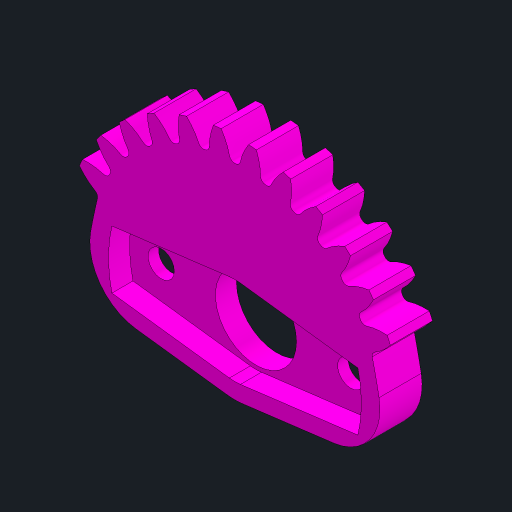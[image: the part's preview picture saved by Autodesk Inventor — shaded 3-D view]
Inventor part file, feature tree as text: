
AUTODESK INVENTOR PART (.ipt)
format: ipt  version: 2023.2 (Build 272271030, 271C)  size: 692,736 bytes
history: native  units: mm
features: extrude x5, sketch x4, pattern_circular x1, hole x1, projected_geometry x1
ambient origin geometry x8: Origin, YZ Plane, XZ Plane, XY Plane, X Axis, Y Axis, Z Axis, Center Point
bodies: Solid1 (feature_tree)
feature tree (12):
  sketch  "Sketch1"  dims[d0=4.0mm d1=0.0mm d2=0.0mm d3=0.0mm]
  extrude  "Extrusion1"  TaperAngle=0.0deg  [1 undecoded]
  extrude  "Extrusion2"  Depth=8.0mm
  pattern_circular  "Circular Pattern1"  [2 undecoded]
  extrude  "Extrusion3"  Depth=5.0mm
  extrude  "Extrusion4"  Depth=5.0mm
  hole  "Hole1"  [1 undecoded]
  extrude  "Extrusion5"  Depth=5.0mm TaperAngle=0.0deg
  sketch  "Sketch2"  dims[d4=300.0mm d5=360.0deg d7=8.0mm]
  sketch  "Sketch3"  dims[d8=32.0mm]
  sketch  "Sketch4"  dims[d9=4.0mm d10=4.0mm d11=4.0mm d12=0.2mm d13=24.0mm d14=2.0mm d15=0.0mm d16=0.0mm d17=0.0mm d18=18.0mm d19=9.0mm d20=2.5mm d21=6.0mm d22=6.0mm d23=1.0mm d24=90.0deg d25=8.0mm d26=20.594885mm d27=1.5mm d28=5.0mm d29=0.0mm d30=0.0mm d31=7.7mm]
  projected_geometry  "Projected Loop2"
note: 4 required parameter values undecoded (feature->parameter linkage not recoverable at this tier; creation-order binding heuristic only, values carry confidence <= 0.55)
